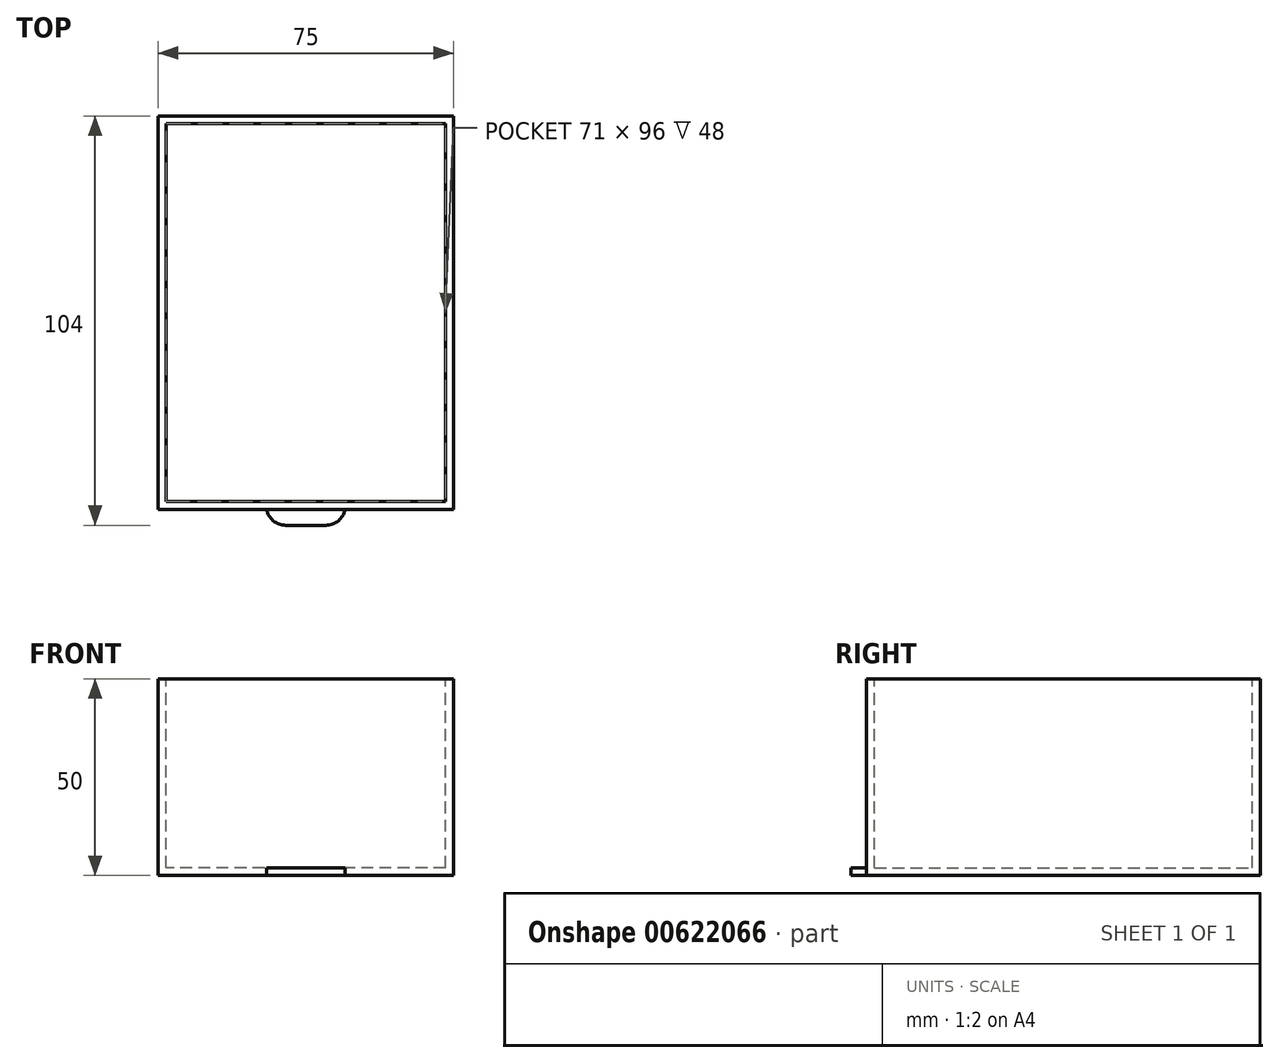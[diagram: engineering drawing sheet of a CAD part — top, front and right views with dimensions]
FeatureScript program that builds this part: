
annotation { "Feature Type Name" : "Feature", "Feature Type Description" : "" }
export const myFeature = defineFeature(function(context is Context, id is Id, definition is map)
    precondition{}
    {
        {
            assignVariable(context, id + "F0", {"name" : "wand", "anyValue" : 2});
        }
        {
            assignVariable(context, id + "F1", {"name" : "h", "anyValue" : 50});
        }
        {
            var Q0;
            Q0=qCreatedBy(makeId("Top.planeOp"),FACE);
            var sketch = newSketch(context, id + "F2", { "sketchPlane" : qUnion([Q0])});
            skLineSegment(sketch, "E0.bottom", {"start": v(37.5, -50) * mm, "end": v(-37.5, -50) * mm});
            skLineSegment(sketch, "E0.top", {"start": v(37.5, 50) * mm, "end": v(-37.5, 50) * mm});
            skLineSegment(sketch, "E0.left", {"start": v(37.5, -50) * mm, "end": v(37.5, 50) * mm});
            skLineSegment(sketch, "E0.right", {"start": v(-37.5, -50) * mm, "end": v(-37.5, 50) * mm});
            skPoint(sketch, "E0.middle", {"position": v(0, 0) * mm});
            skSolve(sketch);
        }
        {
            var Q0;
            Q0 = qSketchRegion(id + "F2", true);
            extrude(context, id + "F3", {"entities" : qUnion([Q0]), "oppositeDirection" : true, "depth" : (getVariable(context, 'h')) * mm, "offsetDistance" : 25 * mm});
        }
        {
            var Q0;
            Q0=makeQuery(id+"F3.opExtrude","CAP_FACE",FACE,{"disambiguationData":[OSD([sQuery(id+"F2.wireOp",EDGE,"E0.bottom"),sQuery(id+"F2.wireOp",EDGE,"E0.top"),sQuery(id+"F2.wireOp",EDGE,"E0.left"),sQuery(id+"F2.wireOp",EDGE,"E0.right")])],"isStart":true});
            shell(context, id + "F4", {"entities" : qUnion([Q0]), "thickness" : (getVariable(context, 'wand')) * mm});
        }
        {
            var Q0;
            Q0=makeQuery(id+"F3.opExtrude","SWEPT_FACE",FACE,{"disambiguationData":[OSD([sQuery(id+"F2.wireOp",EDGE,"E0.bottom")])]});
            var sketch = newSketch(context, id + "F5", { "sketchPlane" : qUnion([Q0])});
            skLineSegment(sketch, "E1.bottom", {"start": v(-10, -50) * mm, "end": v(10, -50) * mm});
            skLineSegment(sketch, "E1.top", {"start": v(-10, -48) * mm, "end": v(10, -48) * mm});
            skLineSegment(sketch, "E1.left", {"start": v(-10, -50) * mm, "end": v(-10, -48) * mm});
            skLineSegment(sketch, "E1.right", {"start": v(10, -50) * mm, "end": v(10, -48) * mm});
            skSolve(sketch);
        }
        {
            var Q0;
            Q0=makeQuery(id+"F5.imprint","IMPRINT",FACE,{"disambiguationData":[TD([[makeQuery(id+"F5.imprint","IMPRINT",EDGE,{"derivedFrom":sQuery(id+"F5.wireOp",EDGE,"E1.bottom")}),-1.0]])]});
            extrude(context, id + "F6", {"entities" : qUnion([Q0]), "operationType" : NewBodyOperationType.ADD, "depth" : 4 * mm, "offsetDistance" : 25 * mm});
        }
        {
            var Q0;
            Q0=makeQuery(id+"F6.opExtrude","CAP_EDGE",EDGE,{"disambiguationData":[OSD([sQuery(id+"F5.wireOp",EDGE,"E1.right")])],"isStart":false});
            var Q1;
            Q1=makeQuery(id+"F6.opExtrude","CAP_EDGE",EDGE,{"disambiguationData":[OSD([sQuery(id+"F5.wireOp",EDGE,"E1.left")])],"isStart":false});
            fillet(context, id + "F7", {"entities" : qUnion([Q0, Q1]), "radius" : 5 * mm, "tangentPropagation" : true, "allowEdgeOverflow" : false});
        }
    });
